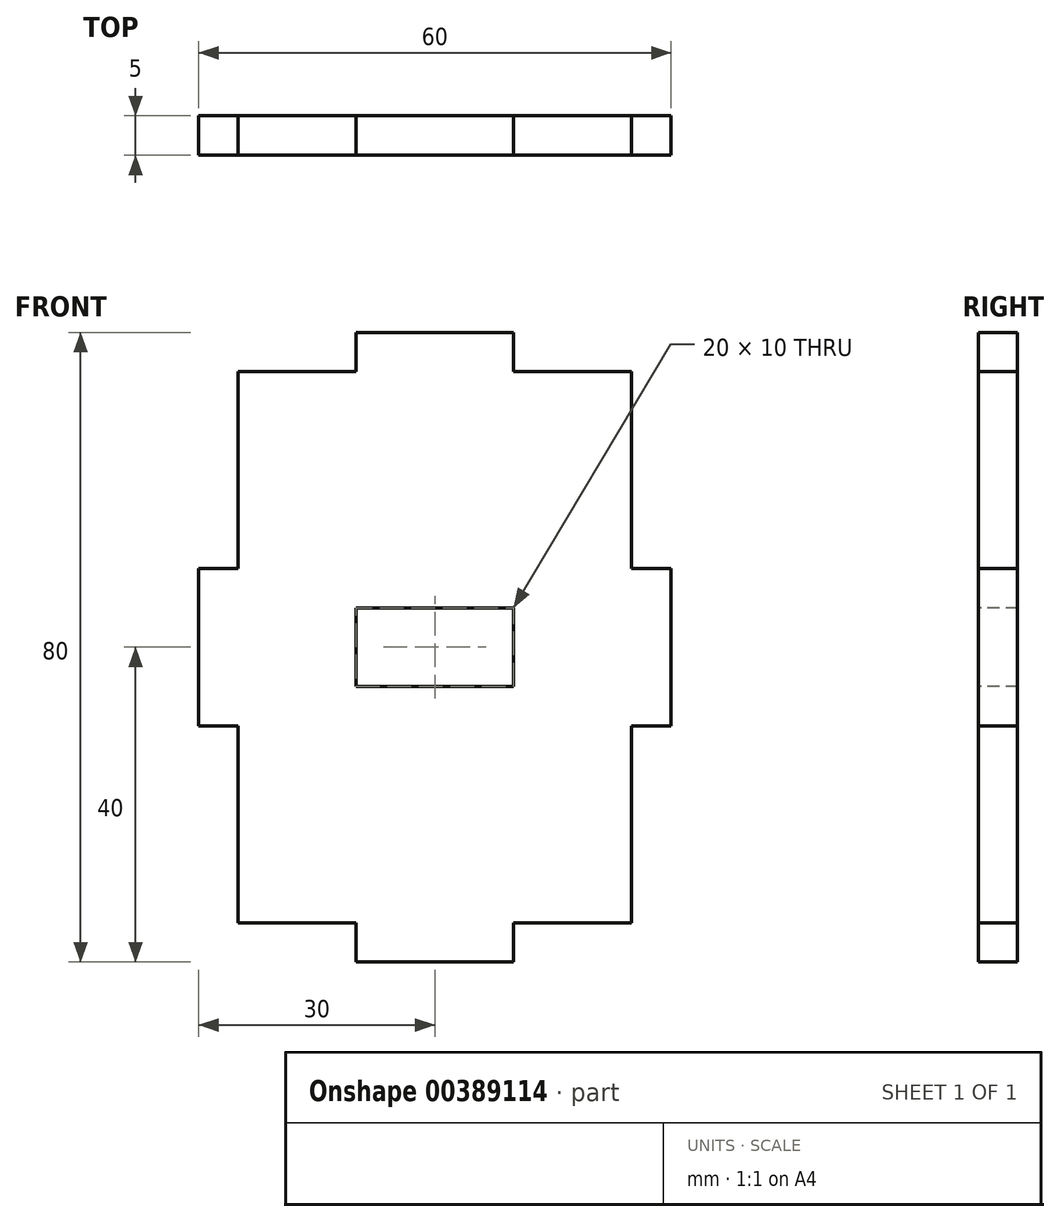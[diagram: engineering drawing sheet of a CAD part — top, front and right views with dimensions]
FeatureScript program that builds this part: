
annotation { "Feature Type Name" : "Feature", "Feature Type Description" : "" }
export const myFeature = defineFeature(function(context is Context, id is Id, definition is map)
    precondition{}
    {
        {
            var Q0;
            Q0=qCreatedBy(makeId("Front.planeOp"),FACE);
            var sketch = newSketch(context, id + "F0", { "sketchPlane" : qUnion([Q0])});
            skLineSegment(sketch, "E0", {"start": v(0, 0) * mm, "end": v(0, 25) * mm});
            skLineSegment(sketch, "E1", {"start": v(0, 25) * mm, "end": v(-5, 25) * mm});
            skLineSegment(sketch, "E2", {"start": v(-5, 25) * mm, "end": v(-5, 45) * mm});
            skLineSegment(sketch, "E3", {"start": v(-5, 45) * mm, "end": v(0, 45) * mm});
            skLineSegment(sketch, "E4", {"start": v(0, 45) * mm, "end": v(0, 70) * mm});
            skLineSegment(sketch, "E5", {"start": v(0, 70) * mm, "end": v(15, 70) * mm});
            skLineSegment(sketch, "E6", {"start": v(15, 70) * mm, "end": v(15, 75) * mm});
            skLineSegment(sketch, "E7", {"start": v(15, 75) * mm, "end": v(35, 75) * mm});
            skLineSegment(sketch, "E8", {"start": v(35, 75) * mm, "end": v(35, 70) * mm});
            skLineSegment(sketch, "E9", {"start": v(35, 70) * mm, "end": v(50, 70) * mm});
            skLineSegment(sketch, "E10", {"start": v(50, 70) * mm, "end": v(50, 45) * mm});
            skLineSegment(sketch, "E11", {"start": v(50, 45) * mm, "end": v(55, 45) * mm});
            skLineSegment(sketch, "E12", {"start": v(55, 45) * mm, "end": v(55, 25) * mm});
            skLineSegment(sketch, "E13", {"start": v(55, 25) * mm, "end": v(50, 25) * mm});
            skLineSegment(sketch, "E14", {"start": v(50, 25) * mm, "end": v(50, 0) * mm});
            skLineSegment(sketch, "E15", {"start": v(50, 0) * mm, "end": v(35, 0) * mm});
            skLineSegment(sketch, "E16", {"start": v(35, 0) * mm, "end": v(35, -5) * mm});
            skLineSegment(sketch, "E17", {"start": v(35, -5) * mm, "end": v(15, -5) * mm});
            skLineSegment(sketch, "E18", {"start": v(15, -5) * mm, "end": v(15, 0) * mm});
            skLineSegment(sketch, "E19", {"start": v(15, 0) * mm, "end": v(0, 0) * mm});
            skSolve(sketch);
        }
        {
            var Q0;
            Q0=makeQuery(id+"F0.imprint","IMPRINT",FACE,{"disambiguationData":[TD([[makeQuery(id+"F0.imprint","IMPRINT",EDGE,{"derivedFrom":sQuery(id+"F0.wireOp",EDGE,"E0")}),-1.0]])]});
            extrude(context, id + "F1", {"entities" : qUnion([Q0]), "depth" : 5 * mm});
        }
        {
            var Q0;
            Q0=makeQuery(id+"F1.opExtrude","CAP_FACE",FACE,{"disambiguationData":[OSD([sQuery(id+"F0.wireOp",EDGE,"E0"),sQuery(id+"F0.wireOp",EDGE,"E1"),sQuery(id+"F0.wireOp",EDGE,"E2"),sQuery(id+"F0.wireOp",EDGE,"E3"),sQuery(id+"F0.wireOp",EDGE,"E4"),sQuery(id+"F0.wireOp",EDGE,"E5"),sQuery(id+"F0.wireOp",EDGE,"E6"),sQuery(id+"F0.wireOp",EDGE,"E7"),sQuery(id+"F0.wireOp",EDGE,"E8"),sQuery(id+"F0.wireOp",EDGE,"E9"),sQuery(id+"F0.wireOp",EDGE,"E10"),sQuery(id+"F0.wireOp",EDGE,"E11"),sQuery(id+"F0.wireOp",EDGE,"E12"),sQuery(id+"F0.wireOp",EDGE,"E13"),sQuery(id+"F0.wireOp",EDGE,"E14"),sQuery(id+"F0.wireOp",EDGE,"E15"),sQuery(id+"F0.wireOp",EDGE,"E16"),sQuery(id+"F0.wireOp",EDGE,"E17"),sQuery(id+"F0.wireOp",EDGE,"E18"),sQuery(id+"F0.wireOp",EDGE,"E19")])],"isStart":false});
            var sketch = newSketch(context, id + "F2", { "sketchPlane" : qUnion([Q0])});
            skLineSegment(sketch, "E20.bottom", {"start": v(15, 40) * mm, "end": v(35, 40) * mm});
            skLineSegment(sketch, "E20.top", {"start": v(15, 30) * mm, "end": v(35, 30) * mm});
            skLineSegment(sketch, "E20.left", {"start": v(15, 40) * mm, "end": v(15, 30) * mm});
            skLineSegment(sketch, "E20.right", {"start": v(35, 40) * mm, "end": v(35, 30) * mm});
            skSolve(sketch);
        }
        {
            var Q0;
            Q0=makeQuery(id+"F2.imprint","IMPRINT",FACE,{"disambiguationData":[TD([[makeQuery(id+"F2.imprint","IMPRINT",EDGE,{"derivedFrom":sQuery(id+"F2.wireOp",EDGE,"E20.bottom")}),-1.0]])]});
            extrude(context, id + "F3", {"entities" : qUnion([Q0]), "operationType" : NewBodyOperationType.REMOVE, "oppositeDirection" : true, "depth" : 25 * mm});
        }
    });
